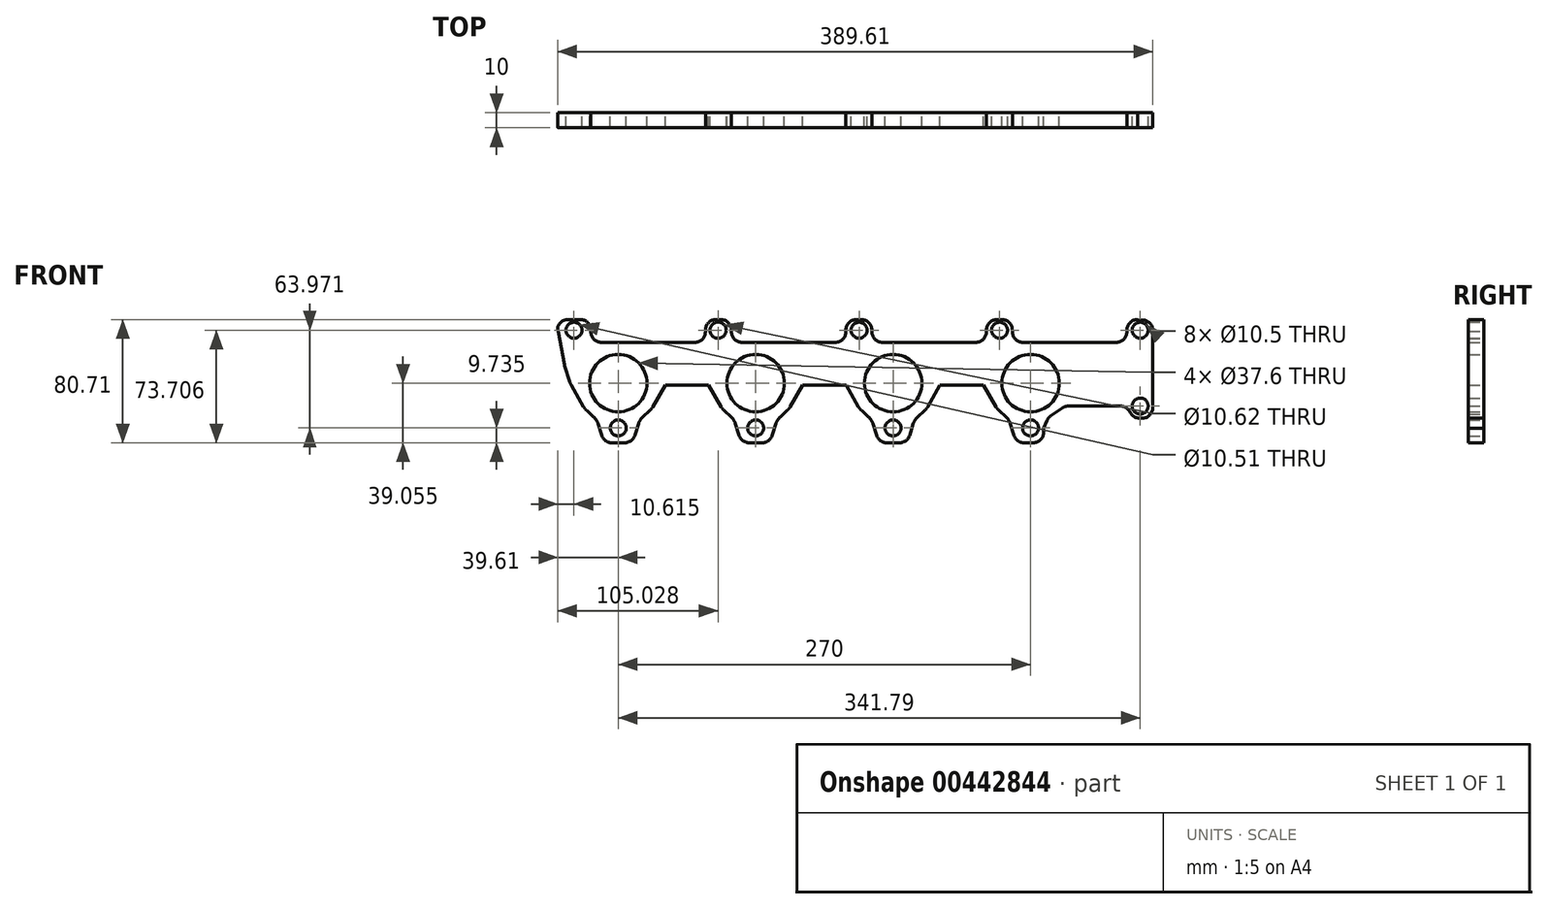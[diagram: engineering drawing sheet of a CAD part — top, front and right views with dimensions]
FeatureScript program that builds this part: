
annotation { "Feature Type Name" : "Feature", "Feature Type Description" : "" }
export const myFeature = defineFeature(function(context is Context, id is Id, definition is map)
    precondition{}
    {
        {
            var Q0;
            Q0=qCreatedBy(makeId("Front.planeOp"),FACE);
            var sketch = newSketch(context, id + "F0", { "sketchPlane" : qUnion([Q0])});
            skLineSegment(sketch, "E0", {"start": v(195, 73.48) * mm, "end": v(195, 23.07) * mm});
            skLineSegment(sketch, "E1", {"start": v(0, 0) * mm, "end": v(0, 80) * mm});
            skLineSegment(sketch, "E2", {"start": v(195, 40) * mm, "end": v(189, 40) * mm, "construction": true});
            skLineSegment(sketch, "E3", {"start": v(189, 40) * mm, "end": v(189, 47.06) * mm, "construction": true});
            skLineSegment(sketch, "E4", {"start": v(189, 40) * mm, "end": v(189, 0) * mm, "construction": true});
            skLineSegment(sketch, "E5", {"start": v(189, 80) * mm, "end": v(189, 55) * mm, "construction": true});
            skLineSegment(sketch, "E6", {"start": v(189, 47.06) * mm, "end": v(189, 37) * mm, "construction": true});
            skLineSegment(sketch, "E7", {"start": v(189, 55) * mm, "end": v(189, 30) * mm});
            skPoint(sketch, "E8.visualSharp", {"position": v(189, 55) * mm});
            skPoint(sketch, "E9.visualSharp", {"position": v(189, 30) * mm});
            skPoint(sketch, "E10.visualSharp", {"position": v(182, 30) * mm});
            skArc(sketch, "E10.filletArc", {"start": v(182, 30) * mm, "mid": v(183.04, 30.08) * mm, "end": v(184.06, 30.3) * mm});
            skPoint(sketch, "E11.visualSharp", {"position": v(137.43, 30.3) * mm});
            skPoint(sketch, "E12.midSnap0", {"position": v(97.5, 40) * mm});
            skLineSegment(sketch, "E13", {"start": v(0, 39.06) * mm, "end": v(0, 39.06) * mm});
            skPoint(sketch, "E14.visualSharp", {"position": v(0, 54.06) * mm});
            skPoint(sketch, "E15.visualSharp", {"position": v(0, 24.06) * mm});
            skLineSegment(sketch, "E16", {"start": v(50, 39.06) * mm, "end": v(50, 39.06) * mm});
            skPoint(sketch, "E17.visualSharp", {"position": v(50, 54.06) * mm});
            skPoint(sketch, "E18.visualSharp", {"position": v(50, 24.06) * mm});
            skLineSegment(sketch, "E19.1.0.2", {"start": v(-90, 39.06) * mm, "end": v(-90, 39.06) * mm});
            skLineSegment(sketch, "E19.1.0.5", {"start": v(-40, 39.06) * mm, "end": v(-40, 39.06) * mm});
            skLineSegment(sketch, "E19.2.0.2", {"start": v(-180, 39.06) * mm, "end": v(-180, 39.06) * mm});
            skLineSegment(sketch, "E19.2.0.5", {"start": v(-130, 39.06) * mm, "end": v(-130, 39.06) * mm});
            skLineSegment(sketch, "E20", {"start": v(137.62, 30.35) * mm, "end": v(142.46, 30.27) * mm});
            skLineSegment(sketch, "E21", {"start": v(189, 54.06) * mm, "end": v(189, 37) * mm});
            skPoint(sketch, "E22.newPointB", {"position": v(140, 39.06) * mm});
            skArc(sketch, "E22.filletArc", {"start": v(137.62, 30.35) * mm, "mid": v(137.27, 30.27) * mm, "end": v(136.99, 30.04) * mm});
            skLineSegment(sketch, "E23", {"start": v(-173, 0) * mm, "end": v(-194.92, 0.7) * mm, "construction": true});
            skLineSegment(sketch, "E24", {"start": v(-172.92, 73.7) * mm, "end": v(-172.92, 72.7) * mm});
            skLineSegment(sketch, "E25", {"start": v(-165.92, 65.7) * mm, "end": v(-104.92, 65.7) * mm});
            skLineSegment(sketch, "E26", {"start": v(-97.92, 72.7) * mm, "end": v(-97.92, 73.7) * mm});
            skPoint(sketch, "E27.visualSharp", {"position": v(-172.92, 80.7) * mm});
            skArc(sketch, "E27.filletArc", {"start": v(-172.92, 79.93) * mm, "mid": v(-173.15, 80.48) * mm, "end": v(-173.7, 80.7) * mm, "construction": true});
            skLineSegment(sketch, "E28", {"start": v(-194.92, 80.7) * mm, "end": v(-179.92, 80.7) * mm});
            skLineSegment(sketch, "E29", {"start": v(-172.92, 79.93) * mm, "end": v(-172.92, 65.7) * mm});
            skPoint(sketch, "E30.visualSharp", {"position": v(-194.92, 80.7) * mm});
            skArc(sketch, "E30.filletArc", {"start": v(-187.92, 80.7) * mm, "mid": v(-191.62, 79.64) * mm, "end": v(-194.2, 76.78) * mm});
            skArc(sketch, "E31.filletArc", {"start": v(-172.92, 73.7) * mm, "mid": v(-174.97, 78.66) * mm, "end": v(-179.92, 80.7) * mm});
            skPoint(sketch, "E32.visualSharp", {"position": v(-172.92, 65.7) * mm});
            skArc(sketch, "E32.filletArc", {"start": v(-172.92, 72.7) * mm, "mid": v(-170.87, 67.76) * mm, "end": v(-165.92, 65.7) * mm});
            skPoint(sketch, "E33.visualSharp", {"position": v(-97.92, 65.7) * mm});
            skArc(sketch, "E33.filletArc", {"start": v(-104.92, 65.7) * mm, "mid": v(-99.97, 67.76) * mm, "end": v(-97.92, 72.7) * mm});
            skPoint(sketch, "E34.newPointA", {"position": v(-195, 80) * mm});
            skPoint(sketch, "E34.newPointB", {"position": v(-97.92, 80.7) * mm});
            skArc(sketch, "E34.filletArc", {"start": v(-90.92, 80.7) * mm, "mid": v(-95.87, 78.66) * mm, "end": v(-97.92, 73.7) * mm});
            skCircle(sketch, "E35", {"center": v(-184, 73.7) * mm, "radius": 5.25 * mm});
            skPoint(sketch, "E36.startSnap0", {"position": v(-155, 24.06) * mm});
            skCircle(sketch, "E37", {"center": v(-155, 9.73) * mm, "radius": 5.25 * mm});
            skPoint(sketch, "E38.newPointA", {"position": v(-195, 0) * mm});
            skPoint(sketch, "E39.newPointA", {"position": v(0, 40) * mm});
            skPoint(sketch, "E40.visualSharp", {"position": v(-87.22, 24.06) * mm});
            skArc(sketch, "E40.filletArc", {"start": v(-87.45, 24.4) * mm, "mid": v(-87.2, 24.07) * mm, "end": v(-86.91, 23.79) * mm});
            skPoint(sketch, "E41.visualSharp", {"position": v(-75.76, 14.1) * mm});
            skArc(sketch, "E41.filletArc", {"start": v(-75.76, 12.8) * mm, "mid": v(-76.02, 13.98) * mm, "end": v(-76.75, 14.96) * mm});
            skLineSegment(sketch, "E42", {"start": v(-65, 24.06) * mm, "end": v(-65, 0) * mm, "construction": true});
            skCircle(sketch, "E43", {"center": v(-65, 9.73) * mm, "radius": 5.25 * mm});
            skLineSegment(sketch, "E44.1.0.0", {"start": v(-73.92, 65.7) * mm, "end": v(-12.92, 65.7) * mm});
            skArc(sketch, "E44.1.0.1", {"start": v(-80.92, 72.7) * mm, "mid": v(-78.87, 67.76) * mm, "end": v(-73.92, 65.7) * mm});
            skArc(sketch, "E44.1.0.2", {"start": v(1.08, 80.7) * mm, "mid": v(-3.87, 78.66) * mm, "end": v(-5.92, 73.7) * mm});
            skArc(sketch, "E44.1.0.3", {"start": v(-80.92, 73.7) * mm, "mid": v(-82.97, 78.66) * mm, "end": v(-87.92, 80.7) * mm});
            skLineSegment(sketch, "E44.1.0.4", {"start": v(-80.92, 73.7) * mm, "end": v(-80.92, 72.7) * mm});
            skArc(sketch, "E44.1.0.5", {"start": v(-12.92, 65.7) * mm, "mid": v(-7.97, 67.76) * mm, "end": v(-5.92, 72.7) * mm});
            skLineSegment(sketch, "E44.1.0.6", {"start": v(-5.92, 72.7) * mm, "end": v(-5.92, 73.7) * mm});
            skLineSegment(sketch, "E44.2.0.0", {"start": v(18.08, 65.7) * mm, "end": v(79.08, 65.7) * mm});
            skArc(sketch, "E44.2.0.1", {"start": v(11.08, 72.7) * mm, "mid": v(13.13, 67.76) * mm, "end": v(18.08, 65.7) * mm});
            skArc(sketch, "E44.2.0.2", {"start": v(93.08, 80.7) * mm, "mid": v(88.13, 78.66) * mm, "end": v(86.08, 73.7) * mm});
            skArc(sketch, "E44.2.0.3", {"start": v(11.08, 73.7) * mm, "mid": v(9.03, 78.66) * mm, "end": v(4.08, 80.7) * mm});
            skLineSegment(sketch, "E44.2.0.4", {"start": v(11.08, 73.7) * mm, "end": v(11.08, 72.7) * mm});
            skArc(sketch, "E44.2.0.5", {"start": v(79.08, 65.7) * mm, "mid": v(84.03, 67.76) * mm, "end": v(86.08, 72.7) * mm});
            skLineSegment(sketch, "E44.2.0.6", {"start": v(86.08, 72.7) * mm, "end": v(86.08, 73.7) * mm});
            skLineSegment(sketch, "E44.3.0.0", {"start": v(110.08, 65.7) * mm, "end": v(171.08, 65.7) * mm});
            skArc(sketch, "E44.3.0.1", {"start": v(103.08, 72.7) * mm, "mid": v(105.13, 67.76) * mm, "end": v(110.08, 65.7) * mm});
            skArc(sketch, "E44.3.0.2", {"start": v(185.08, 80.7) * mm, "mid": v(180.13, 78.66) * mm, "end": v(178.08, 73.7) * mm});
            skArc(sketch, "E44.3.0.3", {"start": v(103.08, 73.7) * mm, "mid": v(101.03, 78.66) * mm, "end": v(96.08, 80.7) * mm});
            skLineSegment(sketch, "E44.3.0.4", {"start": v(103.08, 73.7) * mm, "end": v(103.08, 72.7) * mm});
            skArc(sketch, "E44.3.0.5", {"start": v(171.08, 65.7) * mm, "mid": v(176.03, 67.76) * mm, "end": v(178.08, 72.7) * mm});
            skLineSegment(sketch, "E44.3.0.6", {"start": v(178.08, 72.7) * mm, "end": v(178.08, 73.7) * mm});
            skLineSegment(sketch, "E44.direction1", {"start": v(-165.92, 65.7) * mm, "end": v(-73.92, 65.7) * mm, "construction": true});
            skCircle(sketch, "E45", {"center": v(-89.58, 73.7) * mm, "radius": 5.31 * mm});
            skCircle(sketch, "E46", {"center": v(2.71, 73.7) * mm, "radius": 5.25 * mm});
            skCircle(sketch, "E47", {"center": v(94.71, 73.7) * mm, "radius": 5.25 * mm});
            skLineSegment(sketch, "E48", {"start": v(-90.92, 80.7) * mm, "end": v(-87.92, 80.7) * mm});
            skLineSegment(sketch, "E49", {"start": v(1.08, 80.7) * mm, "end": v(4.08, 80.7) * mm});
            skLineSegment(sketch, "E50", {"start": v(93.08, 80.7) * mm, "end": v(96.08, 80.7) * mm});
            skLineSegment(sketch, "E51", {"start": v(185.08, 80.7) * mm, "end": v(188.5, 80.46) * mm});
            skPoint(sketch, "E52.visualSharp", {"position": v(195, 80) * mm});
            skArc(sketch, "E52.filletArc", {"start": v(195, 73.48) * mm, "mid": v(193.12, 78.25) * mm, "end": v(188.5, 80.46) * mm});
            skLineSegment(sketch, "E53", {"start": v(25, 24.06) * mm, "end": v(25, 0) * mm, "construction": true});
            skCircle(sketch, "E54", {"center": v(25, 9.73) * mm, "radius": 5.25 * mm});
            skLineSegment(sketch, "E55", {"start": v(115, 24.06) * mm, "end": v(115, 0) * mm, "construction": true});
            skCircle(sketch, "E56", {"center": v(115, 9.73) * mm, "radius": 5.25 * mm});
            skCircle(sketch, "E57", {"center": v(186.79, 73.7) * mm, "radius": 5.25 * mm});
            skPoint(sketch, "E57.centerSnap0", {"position": v(186.79, 80.58) * mm});
            skCircle(sketch, "E58", {"center": v(186.79, 24.06) * mm, "radius": 5.25 * mm});
            skLineSegment(sketch, "E59", {"start": v(180, 20.42) * mm, "end": v(180.4, 19.7) * mm});
            skLineSegment(sketch, "E60", {"start": v(186.53, 16.07) * mm, "end": v(188, 16.07) * mm});
            skLineSegment(sketch, "E61", {"start": v(173.86, 24.06) * mm, "end": v(139.73, 24.06) * mm});
            skLineSegment(sketch, "E62", {"start": v(135.86, 22.86) * mm, "end": v(128.35, 17.76) * mm});
            skLineSegment(sketch, "E63", {"start": v(125.8, 14.62) * mm, "end": v(123.68, 9.43) * mm});
            skLineSegment(sketch, "E64", {"start": v(123.68, 9.43) * mm, "end": v(123.68, 7) * mm});
            skPoint(sketch, "E65.visualSharp", {"position": v(178, 24.06) * mm});
            skArc(sketch, "E65.filletArc", {"start": v(180, 20.42) * mm, "mid": v(177.42, 23.08) * mm, "end": v(173.86, 24.06) * mm});
            skPoint(sketch, "E66.visualSharp", {"position": v(182.38, 16.07) * mm});
            skArc(sketch, "E66.filletArc", {"start": v(180.4, 19.7) * mm, "mid": v(182.96, 17.05) * mm, "end": v(186.53, 16.07) * mm});
            skPoint(sketch, "E67.newPointB", {"position": v(195, 0) * mm});
            skArc(sketch, "E67.filletArc", {"start": v(188, 16.07) * mm, "mid": v(192.95, 18.12) * mm, "end": v(195, 23.07) * mm});
            skPoint(sketch, "E68.visualSharp", {"position": v(137.61, 24.06) * mm});
            skArc(sketch, "E68.filletArc", {"start": v(139.73, 24.06) * mm, "mid": v(137.7, 23.75) * mm, "end": v(135.86, 22.86) * mm});
            skPoint(sketch, "E69.visualSharp", {"position": v(126.6, 16.58) * mm});
            skArc(sketch, "E69.filletArc", {"start": v(128.35, 17.76) * mm, "mid": v(126.84, 16.38) * mm, "end": v(125.8, 14.62) * mm});
            skLineSegment(sketch, "E70", {"start": v(-194.87, 74.52) * mm, "end": v(-194.92, 0.7) * mm});
            skPoint(sketch, "E71.visualSharp", {"position": v(-194.87, 74.52) * mm});
            skArc(sketch, "E71.filletArc", {"start": v(-194.2, 76.78) * mm, "mid": v(-194.6, 74.96) * mm, "end": v(-194.13, 73.16) * mm});
            skLineSegment(sketch, "E72", {"start": v(-175.68, 21.14) * mm, "end": v(-171.07, 16.94) * mm});
            skLineSegment(sketch, "E73", {"start": v(-168.27, 12.56) * mm, "end": v(-165.84, 4.89) * mm});
            skPoint(sketch, "E74.visualSharp", {"position": v(-169.08, 15.12) * mm});
            skArc(sketch, "E74.filletArc", {"start": v(-168.27, 12.56) * mm, "mid": v(-169.38, 14.93) * mm, "end": v(-171.07, 16.94) * mm});
            skArc(sketch, "E75.filletArc", {"start": v(-165.84, 4.89) * mm, "mid": v(-163.3, 1.35) * mm, "end": v(-159.17, 0) * mm});
            skPoint(sketch, "E76.visualSharp", {"position": v(-181.83, 50.48) * mm});
            skLineSegment(sketch, "E77", {"start": v(-194.13, 73.16) * mm, "end": v(-190.18, 51.22) * mm});
            skLineSegment(sketch, "E78", {"start": v(-190.03, 50.6) * mm, "end": v(-186.6, 39.63) * mm});
            skLineSegment(sketch, "E79", {"start": v(-185.72, 37.63) * mm, "end": v(-177.61, 23.55) * mm});
            skPoint(sketch, "E80.visualSharp", {"position": v(-190.12, 50.9) * mm});
            skArc(sketch, "E80.filletArc", {"start": v(-190.18, 51.22) * mm, "mid": v(-190.11, 50.91) * mm, "end": v(-190.03, 50.6) * mm});
            skPoint(sketch, "E81.visualSharp", {"position": v(-186.26, 38.59) * mm});
            skArc(sketch, "E81.filletArc", {"start": v(-186.6, 39.63) * mm, "mid": v(-186.2, 38.6) * mm, "end": v(-185.72, 37.63) * mm});
            skPoint(sketch, "E82.visualSharp", {"position": v(-176.83, 22.2) * mm});
            skArc(sketch, "E82.filletArc", {"start": v(-177.61, 23.55) * mm, "mid": v(-176.74, 22.27) * mm, "end": v(-175.68, 21.14) * mm});
            skLineSegment(sketch, "E83.MirrorCS", {"start": v(-124.28, 37.63) * mm, "end": v(-132.39, 23.55) * mm});
            skLineSegment(sketch, "E84.MirrorCS", {"start": v(-134.32, 21.14) * mm, "end": v(-138.93, 16.94) * mm});
            skArc(sketch, "E85.MirrorCS", {"start": v(-132.39, 23.55) * mm, "mid": v(-133.26, 22.27) * mm, "end": v(-134.32, 21.14) * mm});
            skArc(sketch, "E86.MirrorCS", {"start": v(-141.73, 12.56) * mm, "mid": v(-140.62, 14.93) * mm, "end": v(-138.93, 16.94) * mm});
            skLineSegment(sketch, "E87.MirrorCS", {"start": v(-141.73, 12.56) * mm, "end": v(-144.16, 4.89) * mm});
            skArc(sketch, "E88.MirrorCS", {"start": v(-144.16, 4.89) * mm, "mid": v(-146.7, 1.35) * mm, "end": v(-150.83, 0) * mm});
            skLineSegment(sketch, "E89.1.0.0", {"start": v(-34.28, 37.63) * mm, "end": v(-42.39, 23.55) * mm});
            skArc(sketch, "E89.1.0.1", {"start": v(-42.39, 23.55) * mm, "mid": v(-43.26, 22.27) * mm, "end": v(-44.32, 21.14) * mm});
            skLineSegment(sketch, "E89.1.0.2", {"start": v(-44.32, 21.14) * mm, "end": v(-48.93, 16.94) * mm});
            skArc(sketch, "E89.1.0.3", {"start": v(-51.73, 12.56) * mm, "mid": v(-50.62, 14.93) * mm, "end": v(-48.93, 16.94) * mm});
            skLineSegment(sketch, "E89.1.0.4", {"start": v(-51.73, 12.56) * mm, "end": v(-54.16, 4.89) * mm});
            skArc(sketch, "E89.1.0.5", {"start": v(-54.16, 4.89) * mm, "mid": v(-56.7, 1.35) * mm, "end": v(-60.83, 0) * mm});
            skLineSegment(sketch, "E89.2.0.0", {"start": v(55.72, 37.63) * mm, "end": v(47.61, 23.55) * mm});
            skArc(sketch, "E89.2.0.1", {"start": v(47.61, 23.55) * mm, "mid": v(46.74, 22.27) * mm, "end": v(45.68, 21.14) * mm});
            skLineSegment(sketch, "E89.2.0.2", {"start": v(45.68, 21.14) * mm, "end": v(41.07, 16.94) * mm});
            skArc(sketch, "E89.2.0.3", {"start": v(38.27, 12.56) * mm, "mid": v(39.38, 14.93) * mm, "end": v(41.07, 16.94) * mm});
            skLineSegment(sketch, "E89.2.0.4", {"start": v(38.27, 12.56) * mm, "end": v(35.84, 4.89) * mm});
            skArc(sketch, "E89.2.0.5", {"start": v(35.84, 4.89) * mm, "mid": v(33.3, 1.35) * mm, "end": v(29.17, 0) * mm});
            skLineSegment(sketch, "E90.1.0.0", {"start": v(-95.72, 37.63) * mm, "end": v(-87.61, 23.55) * mm});
            skArc(sketch, "E90.1.0.1", {"start": v(-87.61, 23.55) * mm, "mid": v(-86.74, 22.27) * mm, "end": v(-85.68, 21.14) * mm});
            skLineSegment(sketch, "E90.1.0.2", {"start": v(-85.68, 21.14) * mm, "end": v(-81.07, 16.94) * mm});
            skArc(sketch, "E90.1.0.3", {"start": v(-78.27, 12.56) * mm, "mid": v(-79.38, 14.93) * mm, "end": v(-81.07, 16.94) * mm});
            skLineSegment(sketch, "E90.1.0.4", {"start": v(-78.27, 12.56) * mm, "end": v(-75.84, 4.89) * mm});
            skArc(sketch, "E90.1.0.5", {"start": v(-75.84, 4.89) * mm, "mid": v(-73.3, 1.35) * mm, "end": v(-69.17, 0) * mm});
            skLineSegment(sketch, "E90.2.0.0", {"start": v(-5.72, 37.63) * mm, "end": v(2.39, 23.55) * mm});
            skArc(sketch, "E90.2.0.1", {"start": v(2.39, 23.55) * mm, "mid": v(3.26, 22.27) * mm, "end": v(4.32, 21.14) * mm});
            skLineSegment(sketch, "E90.2.0.2", {"start": v(4.32, 21.14) * mm, "end": v(8.93, 16.94) * mm});
            skArc(sketch, "E90.2.0.3", {"start": v(11.73, 12.56) * mm, "mid": v(10.62, 14.93) * mm, "end": v(8.93, 16.94) * mm});
            skLineSegment(sketch, "E90.2.0.4", {"start": v(11.73, 12.56) * mm, "end": v(14.16, 4.89) * mm});
            skArc(sketch, "E90.2.0.5", {"start": v(14.16, 4.89) * mm, "mid": v(16.7, 1.35) * mm, "end": v(20.83, 0) * mm});
            skLineSegment(sketch, "E90.3.0.0", {"start": v(84.28, 37.63) * mm, "end": v(92.39, 23.55) * mm});
            skArc(sketch, "E90.3.0.1", {"start": v(92.39, 23.55) * mm, "mid": v(93.26, 22.27) * mm, "end": v(94.32, 21.14) * mm});
            skLineSegment(sketch, "E90.3.0.2", {"start": v(94.32, 21.14) * mm, "end": v(98.93, 16.94) * mm});
            skArc(sketch, "E90.3.0.3", {"start": v(101.73, 12.56) * mm, "mid": v(100.62, 14.93) * mm, "end": v(98.93, 16.94) * mm});
            skLineSegment(sketch, "E90.3.0.4", {"start": v(101.73, 12.56) * mm, "end": v(104.16, 4.89) * mm});
            skArc(sketch, "E90.3.0.5", {"start": v(104.16, 4.89) * mm, "mid": v(106.7, 1.35) * mm, "end": v(110.83, 0) * mm});
            skLineSegment(sketch, "E91", {"start": v(-124.28, 37.63) * mm, "end": v(-95.72, 37.63) * mm});
            skLineSegment(sketch, "E92", {"start": v(-34.28, 37.63) * mm, "end": v(-5.72, 37.63) * mm});
            skLineSegment(sketch, "E93", {"start": v(55.72, 37.63) * mm, "end": v(84.28, 37.63) * mm});
            skLineSegment(sketch, "E94", {"start": v(-159.17, 0) * mm, "end": v(-155, 0) * mm});
            skLineSegment(sketch, "E95", {"start": v(-155, 0) * mm, "end": v(-150.83, 0) * mm});
            skLineSegment(sketch, "E96", {"start": v(-69.17, 0) * mm, "end": v(-60.83, 0) * mm});
            skLineSegment(sketch, "E97", {"start": v(20.83, 0) * mm, "end": v(29.17, 0) * mm});
            skLineSegment(sketch, "E98", {"start": v(110.83, 0) * mm, "end": v(116.68, 0) * mm});
            skPoint(sketch, "E99.visualSharp", {"position": v(123.68, 0) * mm});
            skArc(sketch, "E99.filletArc", {"start": v(116.68, 0) * mm, "mid": v(121.63, 2.05) * mm, "end": v(123.68, 7) * mm});
            skPoint(sketch, "E100.middle", {"position": v(-155, 39.06) * mm});
            skPoint(sketch, "E100.middle.positionSnap0", {"position": v(-155, 54.06) * mm});
            skPoint(sketch, "E100.centerSnap0", {"position": v(-155, 54.06) * mm});
            skCircle(sketch, "E101", {"center": v(-155, 39.06) * mm, "radius": 18.8 * mm});
            skCircle(sketch, "E102", {"center": v(-155, 39.06) * mm, "radius": 16.92 * mm});
            skCircle(sketch, "E103.1.0.0", {"center": v(-65, 39.06) * mm, "radius": 16.92 * mm});
            skCircle(sketch, "E103.1.0.1", {"center": v(-65, 39.06) * mm, "radius": 18.8 * mm});
            skCircle(sketch, "E103.2.0.0", {"center": v(25, 39.06) * mm, "radius": 16.92 * mm});
            skCircle(sketch, "E103.2.0.1", {"center": v(25, 39.06) * mm, "radius": 18.8 * mm});
            skCircle(sketch, "E103.3.0.0", {"center": v(115, 39.06) * mm, "radius": 16.92 * mm});
            skCircle(sketch, "E103.3.0.1", {"center": v(115, 39.06) * mm, "radius": 18.8 * mm});
            skLineSegment(sketch, "E104", {"start": v(0, 0) * mm, "end": v(-169.42, 0) * mm, "construction": true});
            skLineSegment(sketch, "E105", {"start": v(-155, 39.06) * mm, "end": v(-155, 0) * mm, "construction": true});
            skLineSegment(sketch, "E106", {"start": v(-155, 39.06) * mm, "end": v(0, 39.06) * mm, "construction": true});
            skSolve(sketch);
        }
        {
            var Q0;
            Q0 = qSketchRegion(id + "F0", true);
            extrude(context, id + "F1", {"entities" : qUnion([Q0]), "depth" : 10 * mm, "offsetDistance" : 25 * mm});
        }
    });
